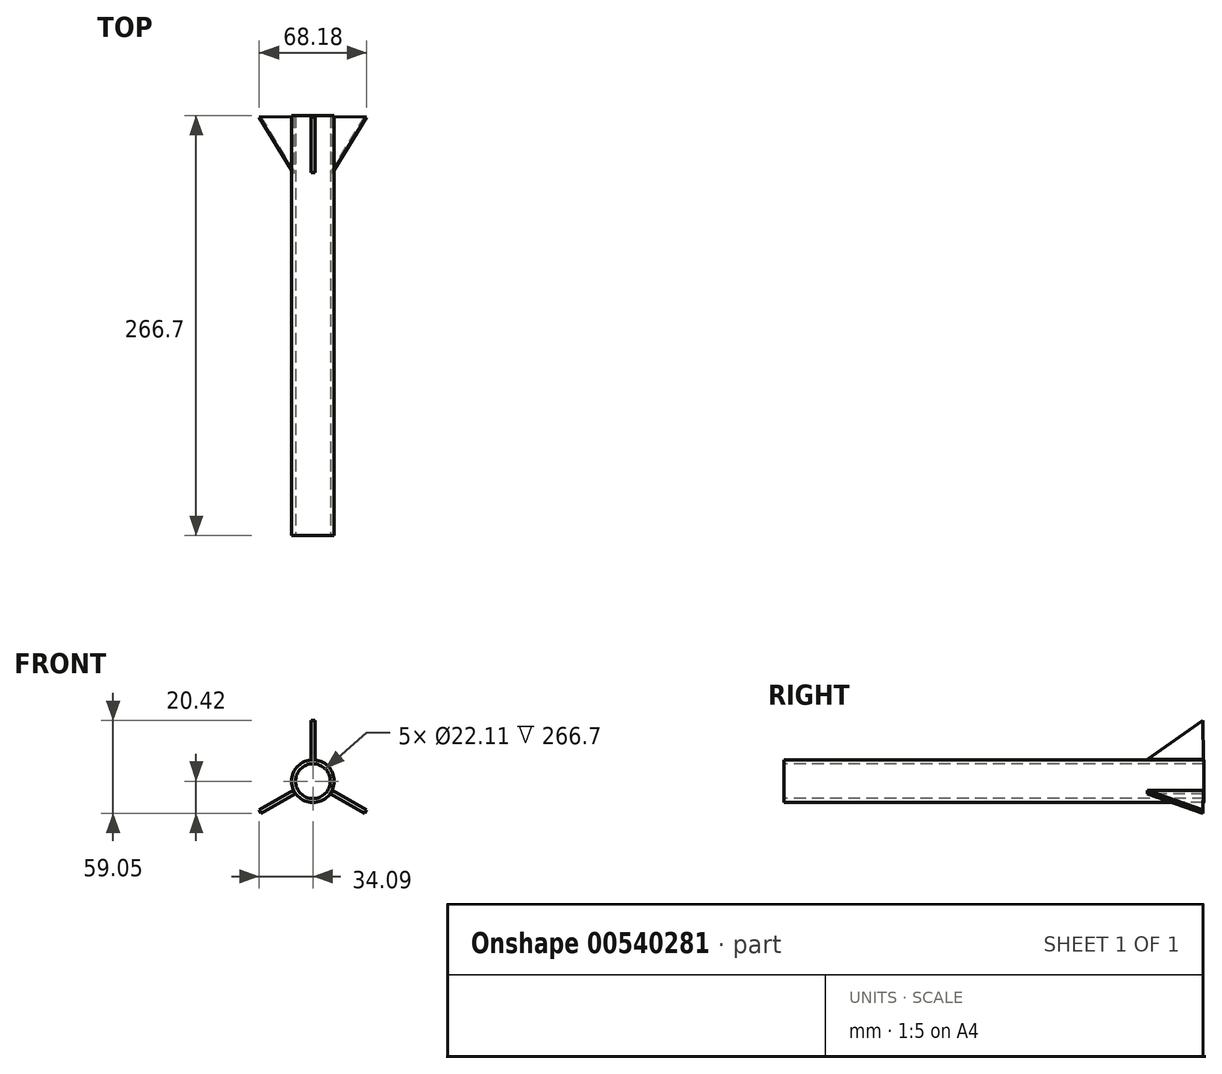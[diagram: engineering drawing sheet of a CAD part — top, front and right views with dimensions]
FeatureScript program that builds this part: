
annotation { "Feature Type Name" : "Feature", "Feature Type Description" : "" }
export const myFeature = defineFeature(function(context is Context, id is Id, definition is map)
    precondition{}
    {
        {
            var Q0;
            Q0=qCreatedBy(makeId("Front.planeOp"),FACE);
            var sketch = newSketch(context, id + "F0", { "sketchPlane" : qUnion([Q0])});
            skCircle(sketch, "E0", {"center": v(0, 0) * mm, "radius": 13.53 * mm});
            skSolve(sketch);
        }
        {
            var Q0;
            Q0 = qSketchRegion(id + "F0", true);
            extrude(context, id + "F1", {"entities" : qUnion([Q0]), "endBound" : BoundingType.SYMMETRIC, "oppositeDirection" : true, "depth" : 266.7 * mm, "offsetDistance" : 25.4 * mm});
        }
        {
            var Q0;
            Q0=qCreatedBy(makeId("Front.planeOp"),FACE);
            var sketch = newSketch(context, id + "F2", { "sketchPlane" : qUnion([Q0])});
            skCircle(sketch, "E1", {"center": v(0, 0) * mm, "radius": 11.06 * mm});
            skSolve(sketch);
        }
        {
            var Q0;
            Q0 = qSketchRegion(id + "F2", true);
            extrude(context, id + "F3", {"entities" : qUnion([Q0]), "operationType" : NewBodyOperationType.REMOVE, "endBound" : BoundingType.SYMMETRIC, "oppositeDirection" : true, "depth" : 266.7 * mm, "offsetDistance" : 25.4 * mm});
        }
        {
            var Q0;
            Q0=qCreatedBy(makeId("Right.planeOp"),FACE);
            var sketch = newSketch(context, id + "F4", { "sketchPlane" : qUnion([Q0])});
            skLineSegment(sketch, "E2", {"start": v(132.77, 13.76) * mm, "end": v(97.2, 13.76) * mm});
            skLineSegment(sketch, "E3", {"start": v(97.2, 13.76) * mm, "end": v(132.46, 38.63) * mm});
            skLineSegment(sketch, "E4", {"start": v(132.46, 38.63) * mm, "end": v(132.77, 13.76) * mm});
            skSolve(sketch);
        }
        {
            var Q0;
            Q0=makeQuery(id+"F4.imprint","IMPRINT",FACE,{"disambiguationData":[TD([[makeQuery(id+"F4.imprint","IMPRINT",EDGE,{"derivedFrom":sQuery(id+"F4.wireOp",EDGE,"E2")}),-1.0]])]});
            extrude(context, id + "F5", {"entities" : qUnion([Q0]), "endBound" : BoundingType.SYMMETRIC, "depth" : 2.54 * mm, "offsetDistance" : 25.4 * mm});
        }
        {
            var Q0;
            Q0=makeQuery(id+"F5.opExtrude","SWEPT_BODY",BODY,{"disambiguationData":[OSD([sQuery(id+"F4.wireOp",EDGE,"E2"),sQuery(id+"F4.wireOp",EDGE,"E3"),sQuery(id+"F4.wireOp",EDGE,"E4")])]});
            var Q1;
            Q1=makeQuery(id+"F1.opExtrude","CAP_EDGE",EDGE,{"disambiguationData":[OSD([sQuery(id+"F0.wireOp",EDGE,"E0")])],"isStart":false});
            transform(context, id + "F6", {"entities" : qUnion([Q0]), "transformType" : TransformType.ROTATION, "transformAxis" : qUnion([Q1]), "angle" : 120 * degree, "makeCopy" : true});
        }
        {
            var Q0;
            Q0=makeQuery(id+"F5.opExtrude","SWEPT_BODY",BODY,{"disambiguationData":[OSD([sQuery(id+"F4.wireOp",EDGE,"E2"),sQuery(id+"F4.wireOp",EDGE,"E3"),sQuery(id+"F4.wireOp",EDGE,"E4")])]});
            var Q1;
            Q1=makeQuery(id+"F1.opExtrude","CAP_EDGE",EDGE,{"disambiguationData":[OSD([sQuery(id+"F0.wireOp",EDGE,"E0")])],"isStart":false});
            transform(context, id + "F7", {"entities" : qUnion([Q0]), "transformType" : TransformType.ROTATION, "transformAxis" : qUnion([Q1]), "angle" : 120 * degree, "oppositeDirection" : true, "makeCopy" : true});
        }
    });
